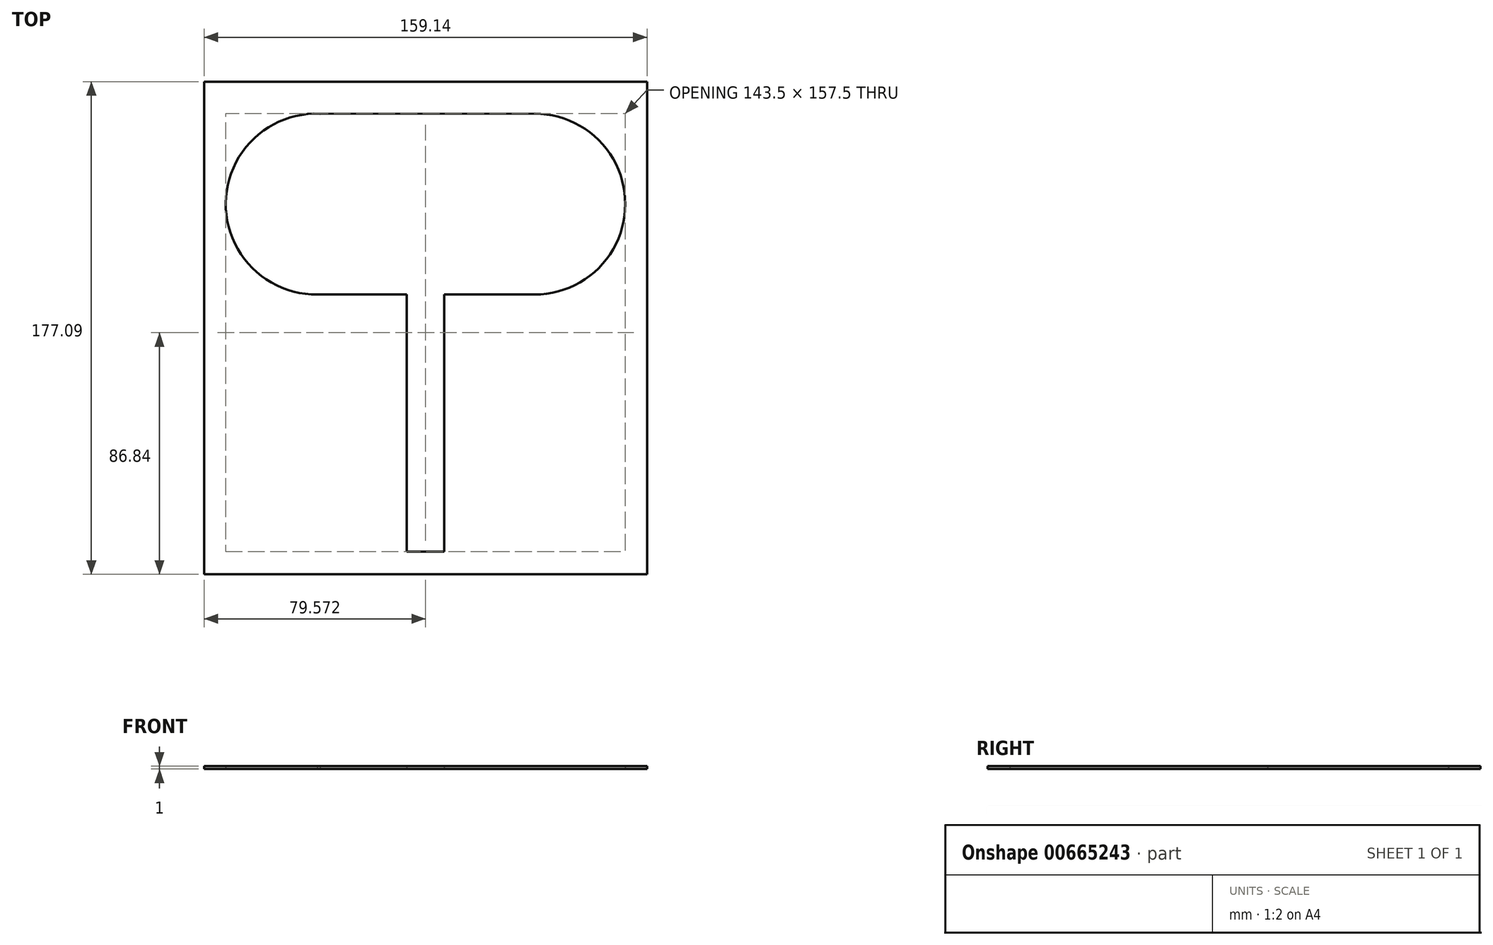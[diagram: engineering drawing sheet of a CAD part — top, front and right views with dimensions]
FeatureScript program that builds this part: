
annotation { "Feature Type Name" : "Feature", "Feature Type Description" : "" }
export const myFeature = defineFeature(function(context is Context, id is Id, definition is map)
    precondition{}
    {
        {
            var Q0;
            Q0=qCreatedBy(makeId("Top.planeOp"),FACE);
            var sketch = newSketch(context, id + "F0", { "sketchPlane" : qUnion([Q0])});
            skLineSegment(sketch, "E0", {"start": v(0, 0) * mm, "end": v(39.25, 0) * mm});
            skCircle(sketch, "E1", {"center": v(39.25, 0) * mm, "radius": 32.5 * mm});
            skLineSegment(sketch, "E2", {"start": v(6.75, 0) * mm, "end": v(6.75, -125) * mm});
            skLineSegment(sketch, "E3", {"start": v(0, 0) * mm, "end": v(0, -182.3) * mm, "construction": true});
            skCircle(sketch, "E4.MirrorC", {"center": v(-39.25, 0) * mm, "radius": 32.5 * mm});
            skLineSegment(sketch, "E5.MirrorCS", {"start": v(0, 0) * mm, "end": v(-39.25, 0) * mm});
            skLineSegment(sketch, "E6.MirrorCS", {"start": v(-6.75, 0) * mm, "end": v(-6.75, -125) * mm});
            skLineSegment(sketch, "E7", {"start": v(-40.61, 32.47) * mm, "end": v(39.24, 32.5) * mm});
            skLineSegment(sketch, "E8", {"start": v(-39.65, -32.5) * mm, "end": v(39.25, -32.5) * mm});
            skLineSegment(sketch, "E9", {"start": v(-6.75, -125) * mm, "end": v(6.75, -125) * mm});
            skLineSegment(sketch, "E10", {"start": v(0, 44) * mm, "end": v(79.57, 44) * mm});
            skLineSegment(sketch, "E11", {"start": v(79.57, 44) * mm, "end": v(79.57, -133.1) * mm});
            skLineSegment(sketch, "E12", {"start": v(79.57, -133.1) * mm, "end": v(0, -133.1) * mm});
            skLineSegment(sketch, "E13.MirrorCS", {"start": v(0, 44) * mm, "end": v(-79.57, 44) * mm});
            skLineSegment(sketch, "E14.MirrorCS", {"start": v(-79.57, 44) * mm, "end": v(-79.57, -133.1) * mm});
            skLineSegment(sketch, "E15.MirrorCS", {"start": v(-79.57, -133.1) * mm, "end": v(0, -133.1) * mm});
            skSolve(sketch);
        }
        {
            var Q0;
            {var subQ9=sQuery(id+"F0.wireOp",EDGE,"E9");Q0=makeQuery(id+"F0.imprint","IMPRINT",FACE,{"disambiguationData":[TD([[makeQuery(id+"F0.imprint","IMPRINT",EDGE,{"derivedFrom":subQ9}),-1.0]])]});}
            extrude(context, id + "F1", {"entities" : qUnion([Q0]), "depth" : 1 * mm, "offsetDistance" : 25 * mm});
        }
    });
